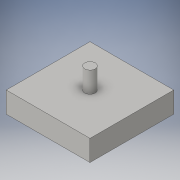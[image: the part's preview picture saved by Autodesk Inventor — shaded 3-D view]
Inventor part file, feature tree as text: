
AUTODESK INVENTOR PART (.ipt)
format: ipt  version: 2016 (Build 200138000, 138)  size: 95,232 bytes
history: native  units: in
note: dims shown in document units (in); Inventor stores cm internally (conversion verified against a paired STEP export)
features: extrude x2, sketch x2
ambient origin geometry x8: Origin, YZ Plane, XZ Plane, XY Plane, X Axis, Y Axis, Z Axis, Center Point
bodies: Solid1 (feature_tree)
feature tree (4):
  extrude  "Extrusion1"  Depth=1.5748in
  extrude  "Extrusion2"  Depth=0.3937in
  sketch  "Sketch1"  dims[d0=1.5748in d1=1.5748in]
  sketch  "Sketch2"  dims[d2=0.3937in d3=0.0in d4=0.1969in d5=0.3937in d6=0.0in]
